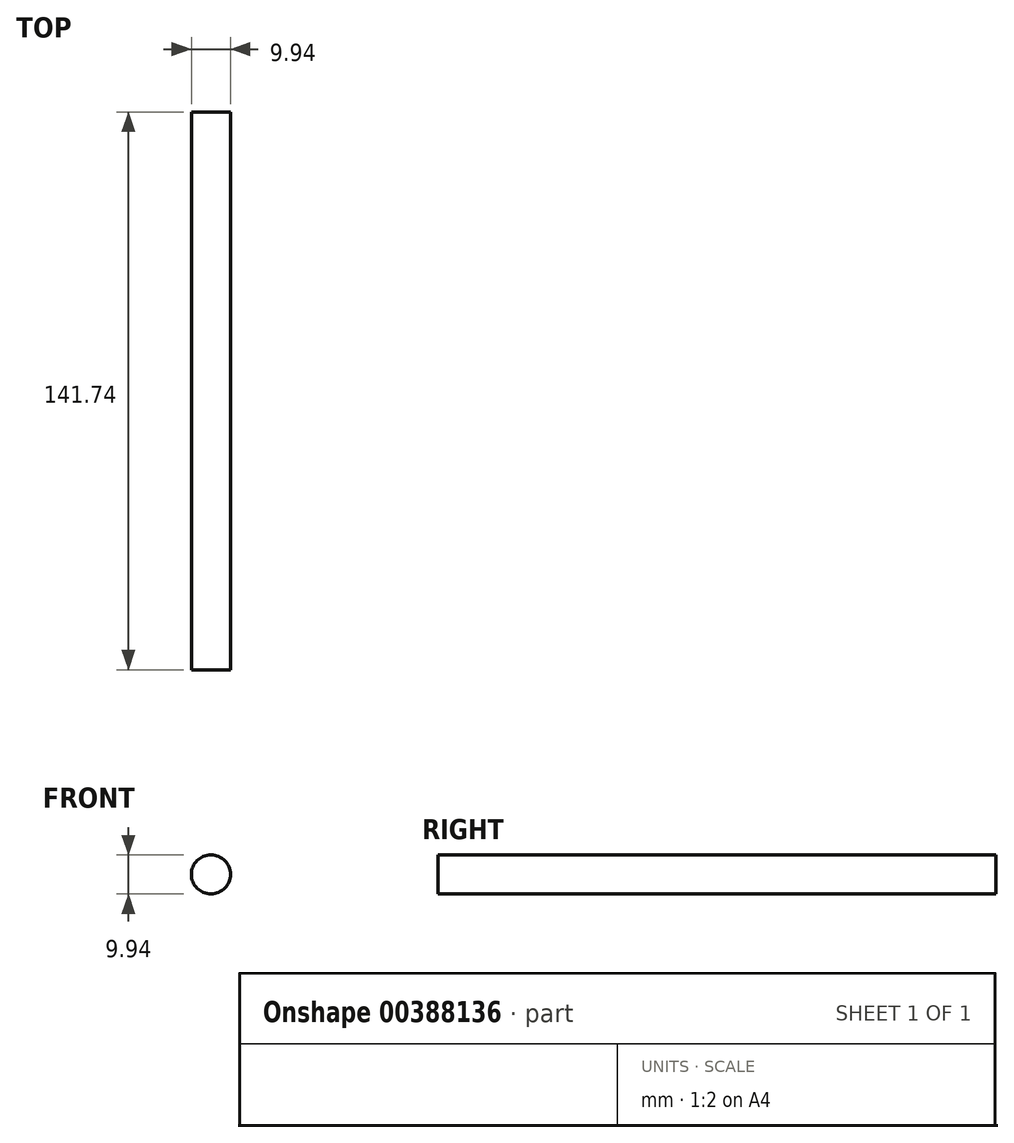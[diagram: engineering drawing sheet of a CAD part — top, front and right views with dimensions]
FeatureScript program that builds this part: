
annotation { "Feature Type Name" : "Feature", "Feature Type Description" : "" }
export const myFeature = defineFeature(function(context is Context, id is Id, definition is map)
    precondition{}
    {
        {
            var Q0;
            Q0=qCreatedBy(makeId("Front.planeOp"),FACE);
            var sketch = newSketch(context, id + "F0", { "sketchPlane" : qUnion([Q0])});
            skCircle(sketch, "E0", {"center": v(0, 0) * mm, "radius": 4.97 * mm});
            skSolve(sketch);
        }
        {
            var Q0;
            Q0=makeQuery(id+"F0.imprint","IMPRINT",FACE,{"disambiguationData":[TD([[makeQuery(id+"F0.imprint","IMPRINT",EDGE,{"derivedFrom":sQuery(id+"F0.wireOp",EDGE,"E0")}),1.0]])]});
            var Q1;
            Q1=sQuery(id+"F0.wireOp",EDGE,"E0");
            extrude(context, id + "F1", {"entities" : qUnion([Q0]), "surfaceEntities" : qUnion([Q1]), "endBound" : BoundingType.SYMMETRIC, "depth" : 141.73 * mm});
        }
    });
